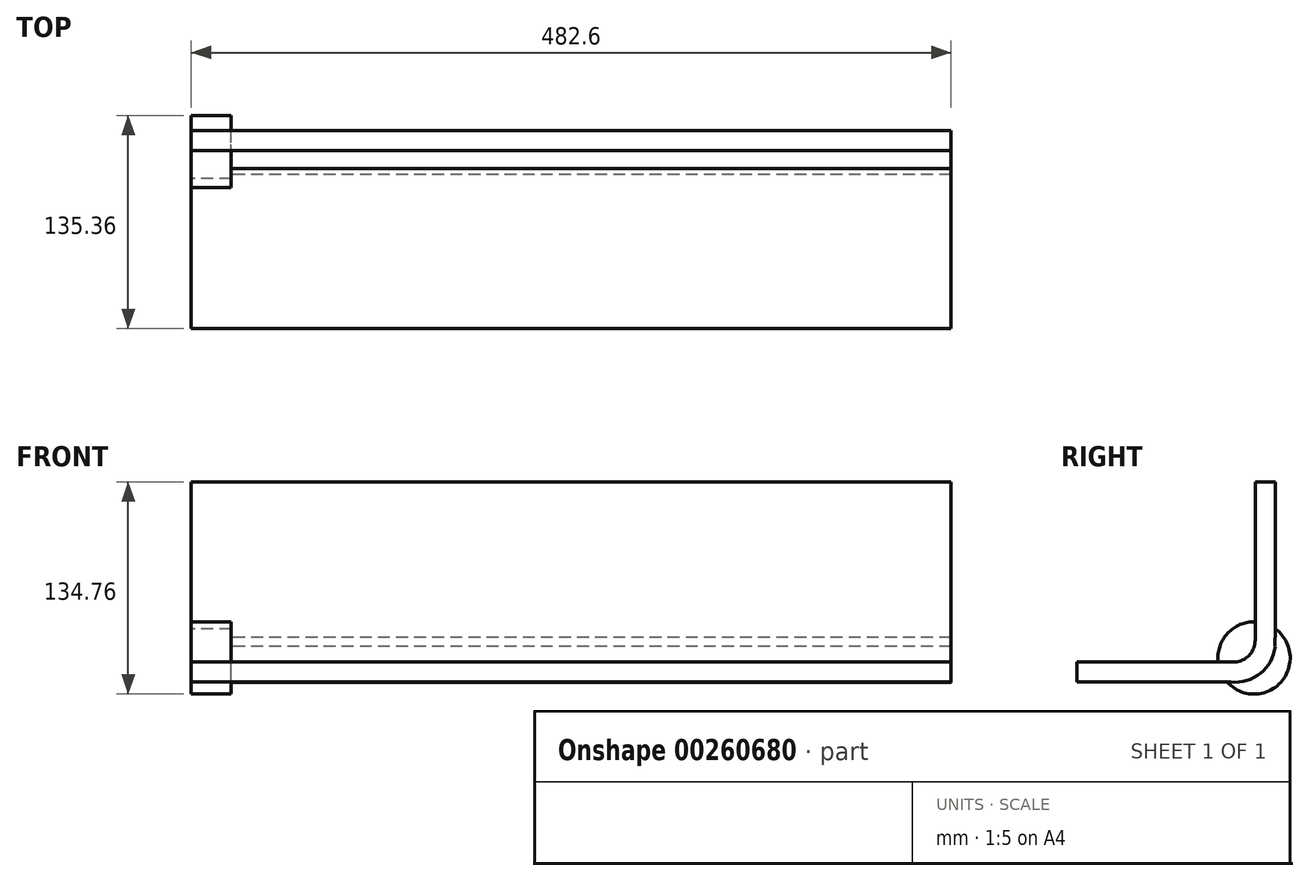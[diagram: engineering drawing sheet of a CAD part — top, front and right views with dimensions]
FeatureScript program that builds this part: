
annotation { "Feature Type Name" : "Feature", "Feature Type Description" : "" }
export const myFeature = defineFeature(function(context is Context, id is Id, definition is map)
    precondition{}
    {
        {
            var Q0;
            Q0=qCreatedBy(makeId("Right.planeOp"),FACE);
            var sketch = newSketch(context, id + "F0", { "sketchPlane" : qUnion([Q0])});
            skLineSegment(sketch, "E0.left", {"start": v(-812.62, 611.3) * mm, "end": v(-812.62, 509.7) * mm});
            skArc(sketch, "E1.trimOffspring", {"start": v(-812.62, 512.69) * mm, "mid": v(-812.8, 509.7) * mm, "end": v(-812.62, 506.73) * mm});
            skArc(sketch, "E2.MirrorCS", {"start": v(-812.62, 512.69) * mm, "mid": v(-819.83, 491.73) * mm, "end": v(-840.7, 484.28) * mm});
            skLineSegment(sketch, "E3.MirrorCS", {"start": v(-836.86, 484.28) * mm, "end": v(-938.46, 484.28) * mm});
            skLineSegment(sketch, "E4.MirrorCS", {"start": v(-836.86, 496.98) * mm, "end": v(-938.46, 496.98) * mm});
            skLineSegment(sketch, "E5.MirrorCS", {"start": v(-938.46, 496.98) * mm, "end": v(-938.46, 484.28) * mm});
            skLineSegment(sketch, "E6.MirrorCS", {"start": v(-812.62, 611.3) * mm, "end": v(-825.32, 611.3) * mm});
            skPoint(sketch, "E7.right.end.orphan", {"position": v(-686.78, 484.28) * mm});
            skPoint(sketch, "E7.right.start.orphan", {"position": v(-686.78, 496.98) * mm});
            skLineSegment(sketch, "E8", {"start": v(-825.32, 611.3) * mm, "end": v(-825.32, 510.91) * mm});
            skArc(sketch, "E9", {"start": v(-836.86, 496.98) * mm, "mid": v(-828.58, 501.87) * mm, "end": v(-825.32, 510.91) * mm});
            skSolve(sketch);
        }
        {
            var Q0;
            {var subQ4=sQuery(id+"F0.wireOp",EDGE,"E0.bottom");Q0=makeQuery(id+"F0.imprint","IMPRINT",FACE,{"disambiguationData":[TD([[makeQuery(id+"F0.imprint","IMPRINT",EDGE,{"derivedFrom":subQ4}),-1.0]])]});}
            var Q1;
            {var subQ4=sQuery(id+"F0.wireOp",EDGE,"E1.trimOffspring");Q1=makeQuery(id+"F0.imprint","IMPRINT",FACE,{"disambiguationData":[TD([[makeQuery(id+"F0.imprint","IMPRINT",EDGE,{"derivedFrom":subQ4}),-1.0]])]});}
            extrude(context, id + "F1", {"entities" : qUnion([Q0, Q1]), "depth" : 482.6 * mm});
        }
        {
            var Q0;
            Q0=qCreatedBy(makeId("Right.planeOp"),FACE);
            var sketch = newSketch(context, id + "F2", { "sketchPlane" : qUnion([Q0])});
            skCircle(sketch, "E10", {"center": v(-826.06, 499.5) * mm, "radius": 22.96 * mm});
            skSolve(sketch);
        }
        {
            var Q0;
            Q0 = qSketchRegion(id + "F2", true);
            extrude(context, id + "F3", {"entities" : qUnion([Q0]), "operationType" : NewBodyOperationType.ADD, "depth" : 25.4 * mm});
        }
    });
